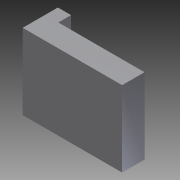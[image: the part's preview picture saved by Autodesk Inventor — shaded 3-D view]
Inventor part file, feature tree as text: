
AUTODESK INVENTOR PART (.ipt)
format: ipt  version: 2011 (Build 150239000, 239)  size: 93,184 bytes
history: native  units: in
note: dims shown in document units (in); Inventor stores cm internally (conversion verified against a paired STEP export)
features: extrude x3, sketch x3
ambient origin geometry x8: Origin, YZ Plane, XZ Plane, XY Plane, X Axis, Y Axis, Z Axis, Center Point
bodies: Solid1 (feature_tree)
feature tree (6):
  extrude  "Extrusion1"  Depth=0.1693in
  extrude  "Extrusion2"  Depth=0.3386in
  extrude  "Extrusion3"  Depth=0.0591in
  sketch  "Sketch1"  dims[d0=0.2283in d1=0.1693in]
  sketch  "Sketch2"  dims[d2=0.4449in d3=0.3386in]
  sketch  "Sketch3"  dims[d4=0.1575in d5=0.0in d6=0.0591in d7=0.0571in d8=0.0in d9=0.0157in d10=0.0157in d11=0.0157in d12=0.0157in d13=0.0315in d14=0.0in]
